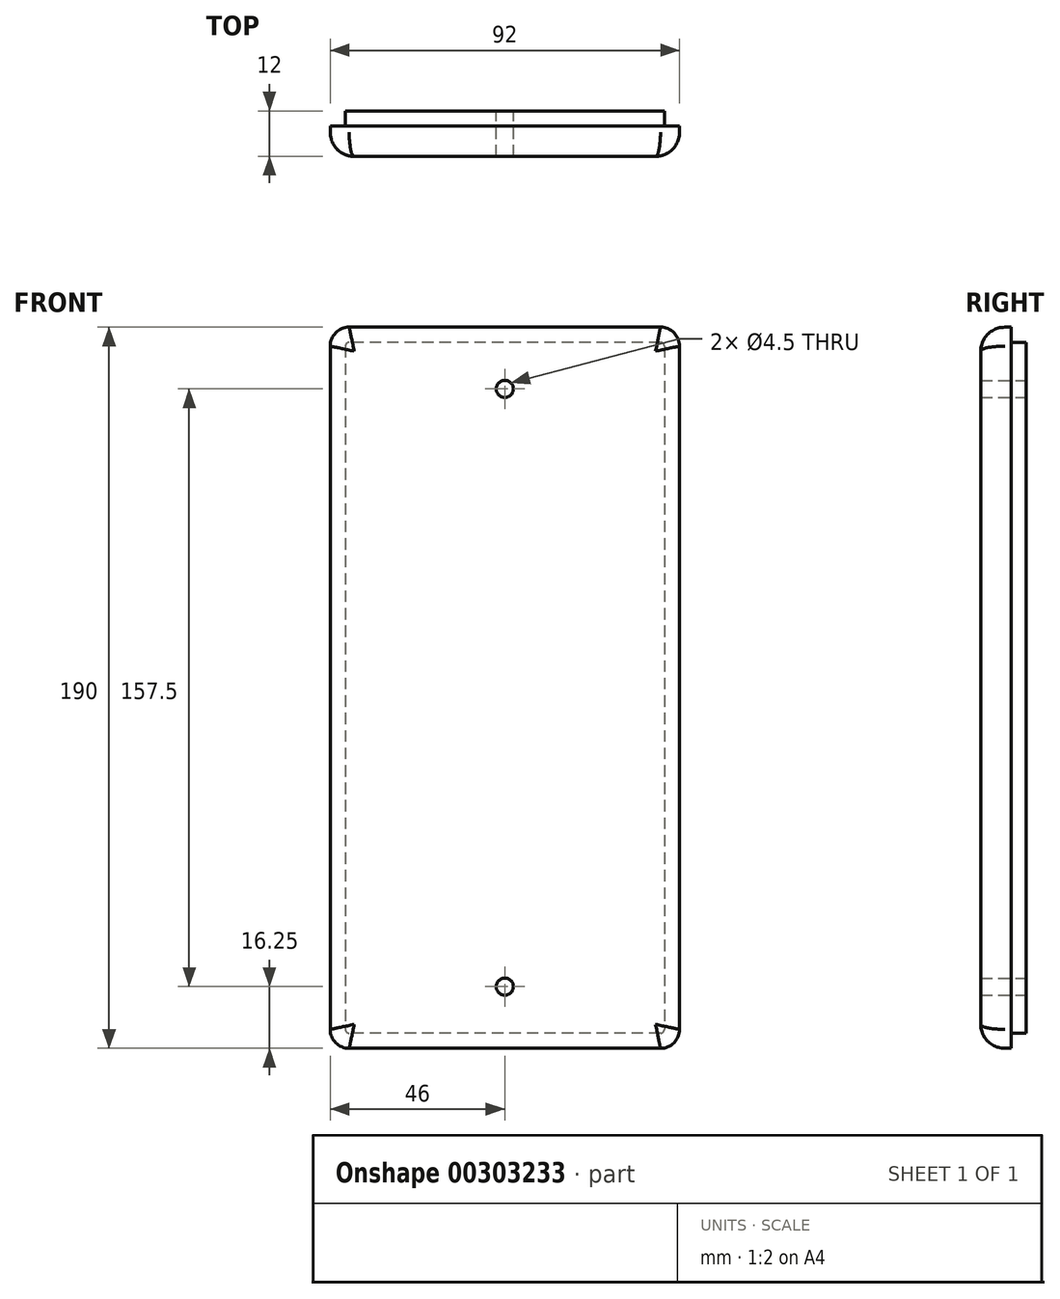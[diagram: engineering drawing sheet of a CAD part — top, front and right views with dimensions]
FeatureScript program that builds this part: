
annotation { "Feature Type Name" : "Feature", "Feature Type Description" : "" }
export const myFeature = defineFeature(function(context is Context, id is Id, definition is map)
    precondition{}
    {
        {
            var Q0;
            Q0=qCreatedBy(makeId("Front.planeOp"),FACE);
            var sketch = newSketch(context, id + "F0", { "sketchPlane" : qUnion([Q0])});
            skLineSegment(sketch, "E0.bottom", {"start": v(41, 95) * mm, "end": v(-41, 95) * mm});
            skLineSegment(sketch, "E0.top", {"start": v(41, -95) * mm, "end": v(-41, -95) * mm});
            skLineSegment(sketch, "E0.left", {"start": v(46, 90) * mm, "end": v(46, -90) * mm});
            skLineSegment(sketch, "E0.right", {"start": v(-46, 90) * mm, "end": v(-46, -90) * mm});
            skPoint(sketch, "E0.middle", {"position": v(0, 0) * mm});
            skPoint(sketch, "E1.visualSharp", {"position": v(46, 95) * mm});
            skArc(sketch, "E1.filletArc", {"start": v(46, 90) * mm, "mid": v(44.54, 93.54) * mm, "end": v(41, 95) * mm});
            skPoint(sketch, "E2.visualSharp", {"position": v(46, -95) * mm});
            skArc(sketch, "E2.filletArc", {"start": v(41, -95) * mm, "mid": v(44.54, -93.54) * mm, "end": v(46, -90) * mm});
            skPoint(sketch, "E3.visualSharp", {"position": v(-46, -95) * mm});
            skArc(sketch, "E3.filletArc", {"start": v(-46, -90) * mm, "mid": v(-44.54, -93.54) * mm, "end": v(-41, -95) * mm});
            skPoint(sketch, "E4.visualSharp", {"position": v(-46, 95) * mm});
            skArc(sketch, "E4.filletArc", {"start": v(-41, 95) * mm, "mid": v(-44.54, 93.54) * mm, "end": v(-46, 90) * mm});
            skCircle(sketch, "E5", {"center": v(0, 78.75) * mm, "radius": 2.25 * mm});
            skCircle(sketch, "E6", {"center": v(0, -78.75) * mm, "radius": 2.25 * mm});
            skLineSegment(sketch, "E7", {"start": v(0, 78.75) * mm, "end": v(0, 0) * mm, "construction": true});
            skLineSegment(sketch, "E8", {"start": v(0, 0) * mm, "end": v(0, -78.75) * mm, "construction": true});
            skSolve(sketch);
        }
        {
            var Q0;
            Q0=makeQuery(id+"F0.imprint","IMPRINT",FACE,{"disambiguationData":[TD([[makeQuery(id+"F0.imprint","IMPRINT",EDGE,{"derivedFrom":sQuery(id+"F0.wireOp",EDGE,"E0.bottom")}),1.0]])]});
            extrude(context, id + "F1", {"entities" : qUnion([Q0]), "depth" : 12 * mm});
        }
        {
            var Q0;
            Q0=makeQuery(id+"F1.opExtrude","CAP_EDGE",EDGE,{"disambiguationData":[OSD([sQuery(id+"F0.wireOp",EDGE,"E0.left")])],"isStart":false});
            fillet(context, id + "F2", {"entities" : qUnion([Q0]), "radius" : 6.3 * mm, "tangentPropagation" : true, "allowEdgeOverflow" : false});
        }
        {
            var Q0;
            Q0=makeQuery(id+"F1.opExtrude","CAP_FACE",FACE,{"disambiguationData":[OSD([sQuery(id+"F0.wireOp",EDGE,"E0.bottom"),sQuery(id+"F0.wireOp",EDGE,"E0.top"),sQuery(id+"F0.wireOp",EDGE,"E0.left"),sQuery(id+"F0.wireOp",EDGE,"E0.right"),sQuery(id+"F0.wireOp",EDGE,"E1.filletArc"),sQuery(id+"F0.wireOp",EDGE,"E2.filletArc"),sQuery(id+"F0.wireOp",EDGE,"E3.filletArc"),sQuery(id+"F0.wireOp",EDGE,"E4.filletArc"),sQuery(id+"F0.wireOp",EDGE,"E5"),sQuery(id+"F0.wireOp",EDGE,"E6")])],"isStart":true});
            var sketch = newSketch(context, id + "F3", { "sketchPlane" : qUnion([Q0])});
            skArc(sketch, "E9.0", {"start": v(-42, 90) * mm, "mid": v(-41.7, 90.7) * mm, "end": v(-41, 91) * mm});
            skLineSegment(sketch, "E9.1", {"start": v(-42, 90) * mm, "end": v(-42, -90) * mm});
            skLineSegment(sketch, "E9.2", {"start": v(-41, 91) * mm, "end": v(41, 91) * mm});
            skArc(sketch, "E9.3", {"start": v(-41, -91) * mm, "mid": v(-41.7, -90.7) * mm, "end": v(-42, -90) * mm});
            skArc(sketch, "E9.4", {"start": v(41, 91) * mm, "mid": v(41.7, 90.7) * mm, "end": v(42, 90) * mm});
            skLineSegment(sketch, "E9.5", {"start": v(42, 90) * mm, "end": v(42, -90) * mm});
            skArc(sketch, "E9.6", {"start": v(42, -90) * mm, "mid": v(41.7, -90.7) * mm, "end": v(41, -91) * mm});
            skLineSegment(sketch, "E9.7", {"start": v(-41, -91) * mm, "end": v(41, -91) * mm});
            skSolve(sketch);
        }
        {
            var Q0;
            Q0=makeQuery(id+"F3.imprint","IMPRINT",FACE,{"disambiguationData":[TD([[makeQuery(id+"F3.imprint","IMPRINT",EDGE,{"derivedFrom":sQuery(id+"F3.wireOp",EDGE,"E9.0")}),-1.0]])]});
            extrude(context, id + "F4", {"entities" : qUnion([Q0]), "operationType" : NewBodyOperationType.REMOVE, "oppositeDirection" : true, "depth" : 4 * mm});
        }
    });
